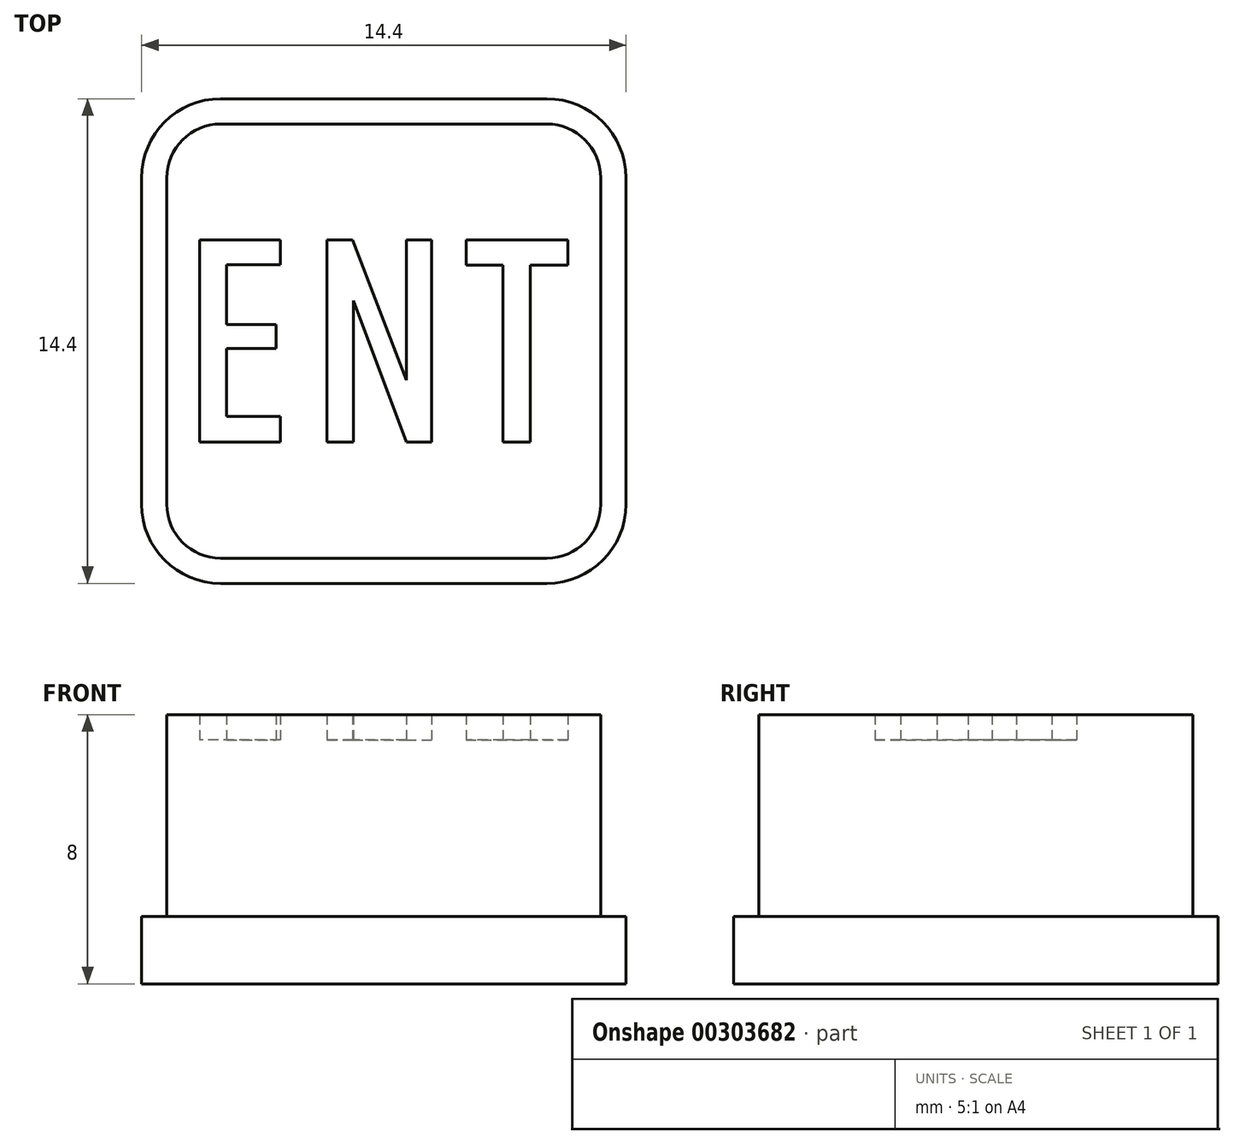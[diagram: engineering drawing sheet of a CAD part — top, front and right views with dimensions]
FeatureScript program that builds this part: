
annotation { "Feature Type Name" : "Feature", "Feature Type Description" : "" }
export const myFeature = defineFeature(function(context is Context, id is Id, definition is map)
    precondition{}
    {
        {
            var Q0;
            Q0=qCreatedBy(makeId("Top.planeOp"),FACE);
            var sketch = newSketch(context, id + "F0", { "sketchPlane" : qUnion([Q0])});
            skArc(sketch, "E0", {"start": v(4.85, -6.45) * mm, "mid": v(5.98, -5.98) * mm, "end": v(6.45, -4.85) * mm});
            skLineSegment(sketch, "E1", {"start": v(6.45, -4.85) * mm, "end": v(6.45, 4.85) * mm});
            skArc(sketch, "E2", {"start": v(6.45, 4.85) * mm, "mid": v(5.98, 5.98) * mm, "end": v(4.85, 6.45) * mm});
            skLineSegment(sketch, "E3", {"start": v(4.85, 6.45) * mm, "end": v(-4.85, 6.45) * mm});
            skArc(sketch, "E4", {"start": v(-4.85, 6.45) * mm, "mid": v(-5.98, 5.98) * mm, "end": v(-6.45, 4.85) * mm});
            skLineSegment(sketch, "E5", {"start": v(-6.45, 4.85) * mm, "end": v(-6.45, -4.85) * mm});
            skArc(sketch, "E6", {"start": v(-6.45, -4.85) * mm, "mid": v(-5.98, -5.98) * mm, "end": v(-4.85, -6.45) * mm});
            skLineSegment(sketch, "E7", {"start": v(-4.85, -6.45) * mm, "end": v(4.85, -6.45) * mm});
            skArc(sketch, "E8", {"start": v(-4.85, 7.2) * mm, "mid": v(-6.51, 6.51) * mm, "end": v(-7.2, 4.85) * mm});
            skLineSegment(sketch, "E9", {"start": v(-7.2, 4.85) * mm, "end": v(-7.2, -4.85) * mm});
            skArc(sketch, "E10", {"start": v(-7.2, -4.85) * mm, "mid": v(-6.51, -6.51) * mm, "end": v(-4.85, -7.2) * mm});
            skLineSegment(sketch, "E11", {"start": v(-4.85, -7.2) * mm, "end": v(4.85, -7.2) * mm});
            skArc(sketch, "E12", {"start": v(4.85, -7.2) * mm, "mid": v(6.51, -6.51) * mm, "end": v(7.2, -4.85) * mm});
            skLineSegment(sketch, "E13", {"start": v(7.2, -4.85) * mm, "end": v(7.2, 4.85) * mm});
            skArc(sketch, "E14", {"start": v(7.2, 4.85) * mm, "mid": v(6.51, 6.51) * mm, "end": v(4.85, 7.2) * mm});
            skLineSegment(sketch, "E15", {"start": v(4.85, 7.2) * mm, "end": v(-4.85, 7.2) * mm});
            skLineSegment(sketch, "E16", {"start": v(-5.47, -3) * mm, "end": v(-5.47, 3) * mm});
            skLineSegment(sketch, "E17", {"start": v(-5.47, 3) * mm, "end": v(-3.08, 3) * mm});
            skLineSegment(sketch, "E18", {"start": v(-3.08, 3) * mm, "end": v(-3.08, 2.27) * mm});
            skLineSegment(sketch, "E19", {"start": v(-3.08, 2.27) * mm, "end": v(-4.67, 2.27) * mm});
            skLineSegment(sketch, "E20", {"start": v(-4.67, 2.27) * mm, "end": v(-4.67, 0.5) * mm});
            skLineSegment(sketch, "E21", {"start": v(-4.67, 0.5) * mm, "end": v(-3.2, 0.5) * mm});
            skLineSegment(sketch, "E22", {"start": v(-3.2, 0.5) * mm, "end": v(-3.2, -0.22) * mm});
            skLineSegment(sketch, "E23", {"start": v(-3.2, -0.22) * mm, "end": v(-4.67, -0.22) * mm});
            skLineSegment(sketch, "E24", {"start": v(-4.67, -0.22) * mm, "end": v(-4.67, -2.24) * mm});
            skLineSegment(sketch, "E25", {"start": v(-4.67, -2.24) * mm, "end": v(-3.08, -2.24) * mm});
            skLineSegment(sketch, "E26", {"start": v(-3.08, -2.24) * mm, "end": v(-3.08, -3) * mm});
            skLineSegment(sketch, "E27", {"start": v(-3.08, -3) * mm, "end": v(-5.47, -3) * mm});
            skLineSegment(sketch, "E28", {"start": v(-1.69, -3) * mm, "end": v(-1.69, 3) * mm});
            skLineSegment(sketch, "E29", {"start": v(-1.69, 3) * mm, "end": v(-0.93, 3) * mm});
            skLineSegment(sketch, "E30", {"start": v(-0.93, 3) * mm, "end": v(0.67, -1.16) * mm});
            skLineSegment(sketch, "E31", {"start": v(0.67, -1.16) * mm, "end": v(0.67, 3) * mm});
            skLineSegment(sketch, "E32", {"start": v(0.67, 3) * mm, "end": v(1.42, 3) * mm});
            skLineSegment(sketch, "E33", {"start": v(1.42, 3) * mm, "end": v(1.42, -3) * mm});
            skLineSegment(sketch, "E34", {"start": v(1.42, -3) * mm, "end": v(0.67, -3) * mm});
            skLineSegment(sketch, "E35", {"start": v(0.67, -3) * mm, "end": v(-0.9, 1.2) * mm});
            skLineSegment(sketch, "E36", {"start": v(-0.9, 1.2) * mm, "end": v(-0.9, -3) * mm});
            skLineSegment(sketch, "E37", {"start": v(-0.9, -3) * mm, "end": v(-1.69, -3) * mm});
            skLineSegment(sketch, "E38", {"start": v(3.55, -3) * mm, "end": v(3.55, 2.26) * mm});
            skLineSegment(sketch, "E39", {"start": v(3.55, 2.26) * mm, "end": v(2.45, 2.26) * mm});
            skLineSegment(sketch, "E40", {"start": v(2.45, 2.26) * mm, "end": v(2.45, 3) * mm});
            skLineSegment(sketch, "E41", {"start": v(2.45, 3) * mm, "end": v(5.47, 3) * mm});
            skLineSegment(sketch, "E42", {"start": v(5.47, 3) * mm, "end": v(5.47, 2.26) * mm});
            skLineSegment(sketch, "E43", {"start": v(5.47, 2.26) * mm, "end": v(4.36, 2.26) * mm});
            skLineSegment(sketch, "E44", {"start": v(4.36, 2.26) * mm, "end": v(4.36, -3) * mm});
            skLineSegment(sketch, "E45", {"start": v(4.36, -3) * mm, "end": v(3.55, -3) * mm});
            skSolve(sketch);
        }
        {
            var Q0;
            Q0=makeQuery(id+"F0.imprint","IMPRINT",FACE,{"disambiguationData":[TD([[makeQuery(id+"F0.imprint","IMPRINT",EDGE,{"derivedFrom":sQuery(id+"F0.wireOp",EDGE,"E0")}),-1.0]])]});
            extrude(context, id + "F1", {"entities" : qUnion([Q0]), "depth" : 2 * mm});
        }
        {
            var Q0;
            Q0=makeQuery(id+"F0.imprint","IMPRINT",FACE,{"disambiguationData":[TD([[makeQuery(id+"F0.imprint","IMPRINT",EDGE,{"derivedFrom":sQuery(id+"F0.wireOp",EDGE,"E0")}),1.0]])]});
            extrude(context, id + "F2", {"entities" : qUnion([Q0]), "operationType" : NewBodyOperationType.ADD, "depth" : 8 * mm});
        }
        {
            var Q0;
            Q0=makeQuery(id+"F0.imprint","IMPRINT",FACE,{"disambiguationData":[TD([[makeQuery(id+"F0.imprint","IMPRINT",EDGE,{"derivedFrom":sQuery(id+"F0.wireOp",EDGE,"E16")}),-1.0]])]});
            var Q1;
            Q1=makeQuery(id+"F0.imprint","IMPRINT",FACE,{"disambiguationData":[TD([[makeQuery(id+"F0.imprint","IMPRINT",EDGE,{"derivedFrom":sQuery(id+"F0.wireOp",EDGE,"E28")}),-1.0]])]});
            var Q2;
            Q2=makeQuery(id+"F0.imprint","IMPRINT",FACE,{"disambiguationData":[TD([[makeQuery(id+"F0.imprint","IMPRINT",EDGE,{"derivedFrom":sQuery(id+"F0.wireOp",EDGE,"E38")}),-1.0]])]});
            extrude(context, id + "F3", {"entities" : qUnion([Q0, Q1, Q2]), "operationType" : NewBodyOperationType.ADD, "depth" : 7.25 * mm});
        }
    });
